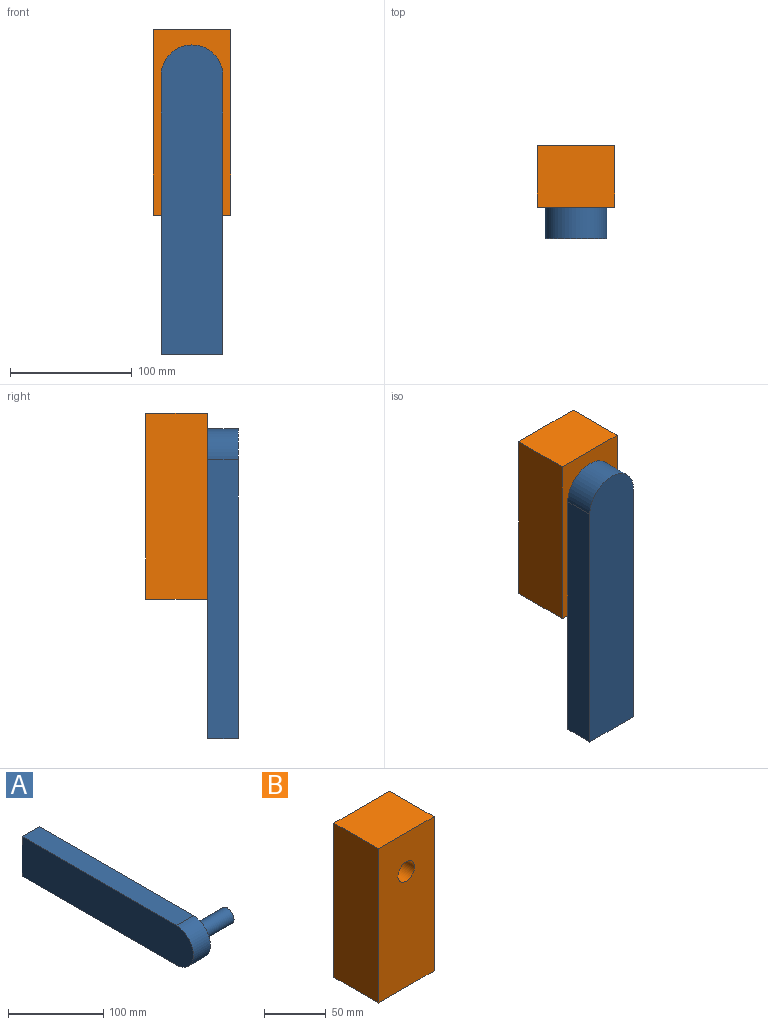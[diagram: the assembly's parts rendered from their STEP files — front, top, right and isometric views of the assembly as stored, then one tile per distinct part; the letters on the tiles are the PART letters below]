
ASSEMBLY  parts=2 mates=1
PART A: 8 faces, bbox 76.2x254x50.8 mm
  f0: plane 50.8x25.4mm, normal (0,1,0), area 1290.3mm2, adj f1,f3,f4,f5
  f1: plane 228.6x25.4mm, normal (0,0,1), area 5806.4mm2, adj f0,f2,f4,f5
  f2: cylinder r=25.4mm len=50.8mm, axis (-1,0,0), area 2026.8mm2, adj f1,f3,f4,f5
  f3: plane 228.6x25.4mm, normal (0,0,-1), area 5806.4mm2, adj f0,f2,f4,f5
  f4: plane 254x50.8mm, normal (1,0,0), area 12341.3mm2, adj f0,f1,f2,f3,f6
  f5: plane 254x50.8mm, normal (-1,0,0), area 12626.3mm2, adj f0,f1,f2,f3
  f6: cylinder r=9.53mm len=50.8mm, axis (-1,0,0), area 3040.2mm2, adj f4,f7
  f7: plane 19.05x19.05mm, normal (1,0,0), area 285mm2, adj f6
PART B: 7 faces, bbox 63.5x50.8x152.4 mm
  f0: plane 63.5x50.8mm, normal (0,0,1), area 3225.8mm2, adj f1,f4,f5,f6
  f1: plane 152.4x50.8mm, normal (-1,0,0), area 7741.9mm2, adj f0,f2,f5,f6
  f2: plane 63.5x50.8mm, normal (0,0,-1), area 3225.8mm2, adj f1,f4,f5,f6
  f3: cylinder r=9.53mm len=50.8mm, axis (0,1,0), area 3040.2mm2, adj f5,f6
  f4: plane 152.4x50.8mm, normal (1,0,0), area 7741.9mm2, adj f0,f2,f5,f6
  f5: plane 152.4x63.5mm, normal (0,-1,0), area 9392.4mm2, adj f0,f1,f2,f3,f4
  f6: plane 152.4x63.5mm, normal (0,1,0), area 9392.4mm2, adj f0,f1,f2,f3,f4
PLACE A rot(axis=(-0.58,-0.58,0.58),120deg) t=(1.14,-76.22,-160.52)mm
PLACE B t=(0.15,-0.02,0.06)mm
MATE revolute A.f2 <-> B.f3  axis (0,1,0) through (0.15,-0.02,-38.12)mm
